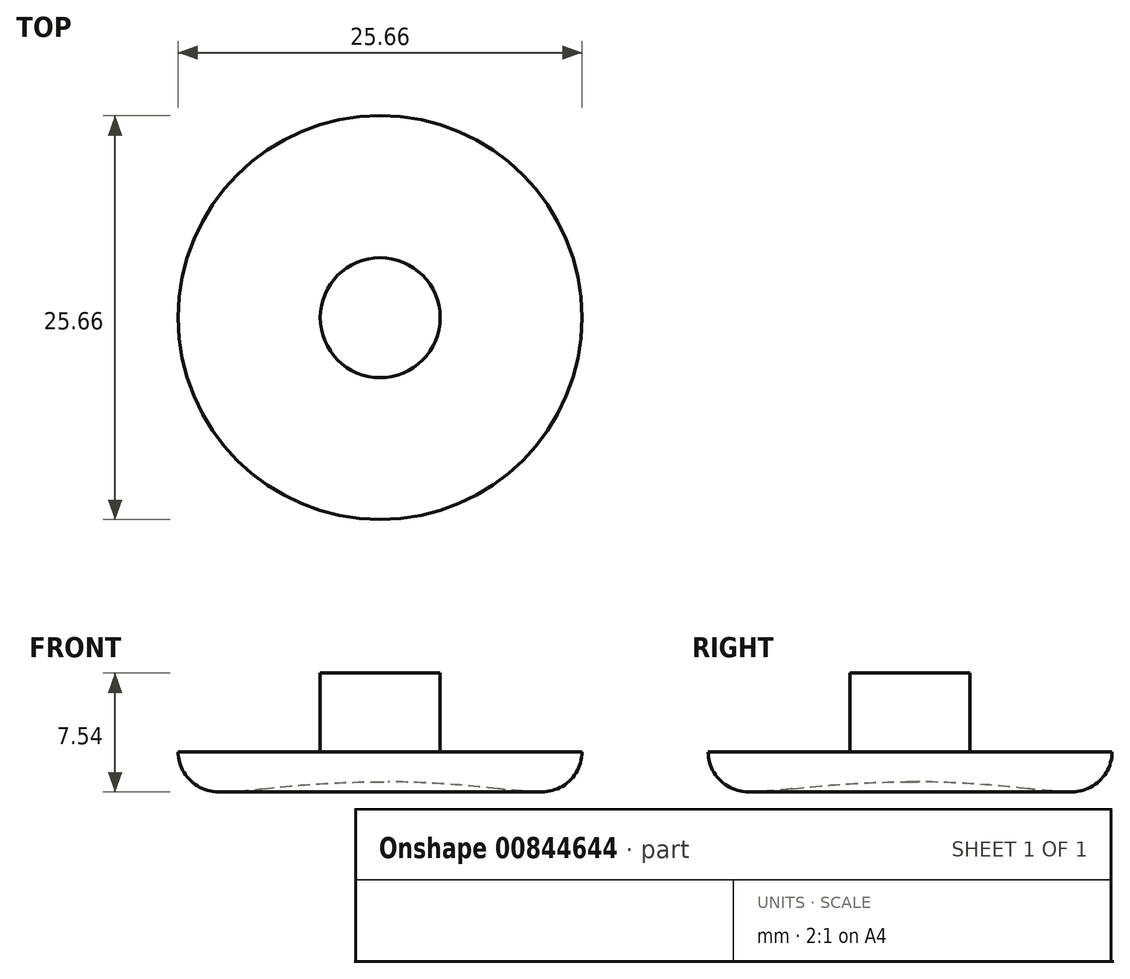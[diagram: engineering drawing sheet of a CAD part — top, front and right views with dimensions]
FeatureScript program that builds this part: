
annotation { "Feature Type Name" : "Feature", "Feature Type Description" : "" }
export const myFeature = defineFeature(function(context is Context, id is Id, definition is map)
    precondition{}
    {
        {
            var Q0;
            Q0=qCreatedBy(makeId("Top.planeOp"),FACE);
            var sketch = newSketch(context, id + "F0", { "sketchPlane" : qUnion([Q0])});
            skCircle(sketch, "E0", {"center": v(0, 0) * mm, "radius": 12.83 * mm});
            skSolve(sketch);
        }
        {
            var Q0;
            Q0=makeQuery(id+"F0.imprint","IMPRINT",FACE,{"disambiguationData":[TD([[makeQuery(id+"F0.imprint","IMPRINT",EDGE,{"derivedFrom":sQuery(id+"F0.wireOp",EDGE,"E0")}),1.0]])]});
            extrude(context, id + "F1", {"entities" : qUnion([Q0]), "oppositeDirection" : true, "depth" : 2.54 * mm, "offsetDistance" : 25.4 * mm});
        }
        {
            var Q0;
            Q0=makeQuery(id+"F1.opExtrude","CAP_FACE",FACE,{"disambiguationData":[OSD([sQuery(id+"F0.wireOp",EDGE,"E0")])],"isStart":false});
            var sketch = newSketch(context, id + "F2", { "sketchPlane" : qUnion([Q0])});
            skCircle(sketch, "E1", {"center": v(0, 0) * mm, "radius": 8.9 * mm});
            skSolve(sketch);
        }
        {
            var Q0;
            Q0=makeQuery(id+"F2.imprint","IMPRINT",FACE,{"disambiguationData":[TD([[makeQuery(id+"F2.imprint","IMPRINT",EDGE,{"derivedFrom":sQuery(id+"F2.wireOp",EDGE,"E1")}),1.0]])]});
            extrude(context, id + "F3", {"entities" : qUnion([Q0]), "operationType" : NewBodyOperationType.REMOVE, "oppositeDirection" : true, "depth" : 0.64 * mm, "offsetDistance" : 25.4 * mm});
        }
        {
            var Q0;
            Q0=makeQuery(id+"F3.boolean.opBoolean","COPY",EDGE,{"derivedFrom":makeQuery(id+"F3.opExtrude","CAP_EDGE",EDGE,{"disambiguationData":[OSD([sQuery(id+"F2.wireOp",EDGE,"E1")])],"isStart":false})});
            fillet(context, id + "F4", {"entities" : qUnion([Q0]), "radius" : 60.96 * mm, "tangentPropagation" : true, "allowEdgeOverflow" : false});
        }
        {
            var Q0;
            Q0=makeQuery(id+"F4.opFillet","BLEND_EDGE",EDGE,{"blendedFrom":[makeQuery(id+"F3.boolean.opBoolean","COPY",EDGE,{"derivedFrom":makeQuery(id+"F3.opExtrude","CAP_EDGE",EDGE,{"disambiguationData":[OSD([sQuery(id+"F2.wireOp",EDGE,"E1")])],"isStart":false})}),makeQuery(id+"F1.opExtrude","CAP_FACE",FACE,{"disambiguationData":[OSD([sQuery(id+"F0.wireOp",EDGE,"E0")])],"isStart":false})],"blendedInto":[makeQuery(id+"F1.opExtrude","CAP_FACE",FACE,{"disambiguationData":[OSD([sQuery(id+"F0.wireOp",EDGE,"E0")])],"isStart":false})]});
            fillet(context, id + "F5", {"entities" : qUnion([Q0]), "radius" : 25.4 * mm, "tangentPropagation" : true, "allowEdgeOverflow" : false});
        }
        {
            var Q0;
            Q0=makeQuery(id+"F1.opExtrude","CAP_EDGE",EDGE,{"disambiguationData":[OSD([sQuery(id+"F0.wireOp",EDGE,"E0")])],"isStart":false});
            fillet(context, id + "F6", {"entities" : qUnion([Q0]), "radius" : 2.54 * mm, "tangentPropagation" : true, "allowEdgeOverflow" : false});
        }
        {
            var Q0;
            Q0=makeQuery(id+"F1.opExtrude","CAP_FACE",FACE,{"disambiguationData":[OSD([sQuery(id+"F0.wireOp",EDGE,"E0")])],"isStart":true});
            var sketch = newSketch(context, id + "F7", { "sketchPlane" : qUnion([Q0])});
            skCircle(sketch, "E2", {"center": v(0, 0) * mm, "radius": 3.81 * mm});
            skSolve(sketch);
        }
        {
            var Q0;
            Q0=makeQuery(id+"F7.imprint","IMPRINT",FACE,{"disambiguationData":[TD([[makeQuery(id+"F7.imprint","IMPRINT",EDGE,{"derivedFrom":sQuery(id+"F7.wireOp",EDGE,"E2")}),1.0]])]});
            extrude(context, id + "F8", {"entities" : qUnion([Q0]), "operationType" : NewBodyOperationType.ADD, "depth" : 5 * mm, "offsetDistance" : 25.4 * mm});
        }
    });
